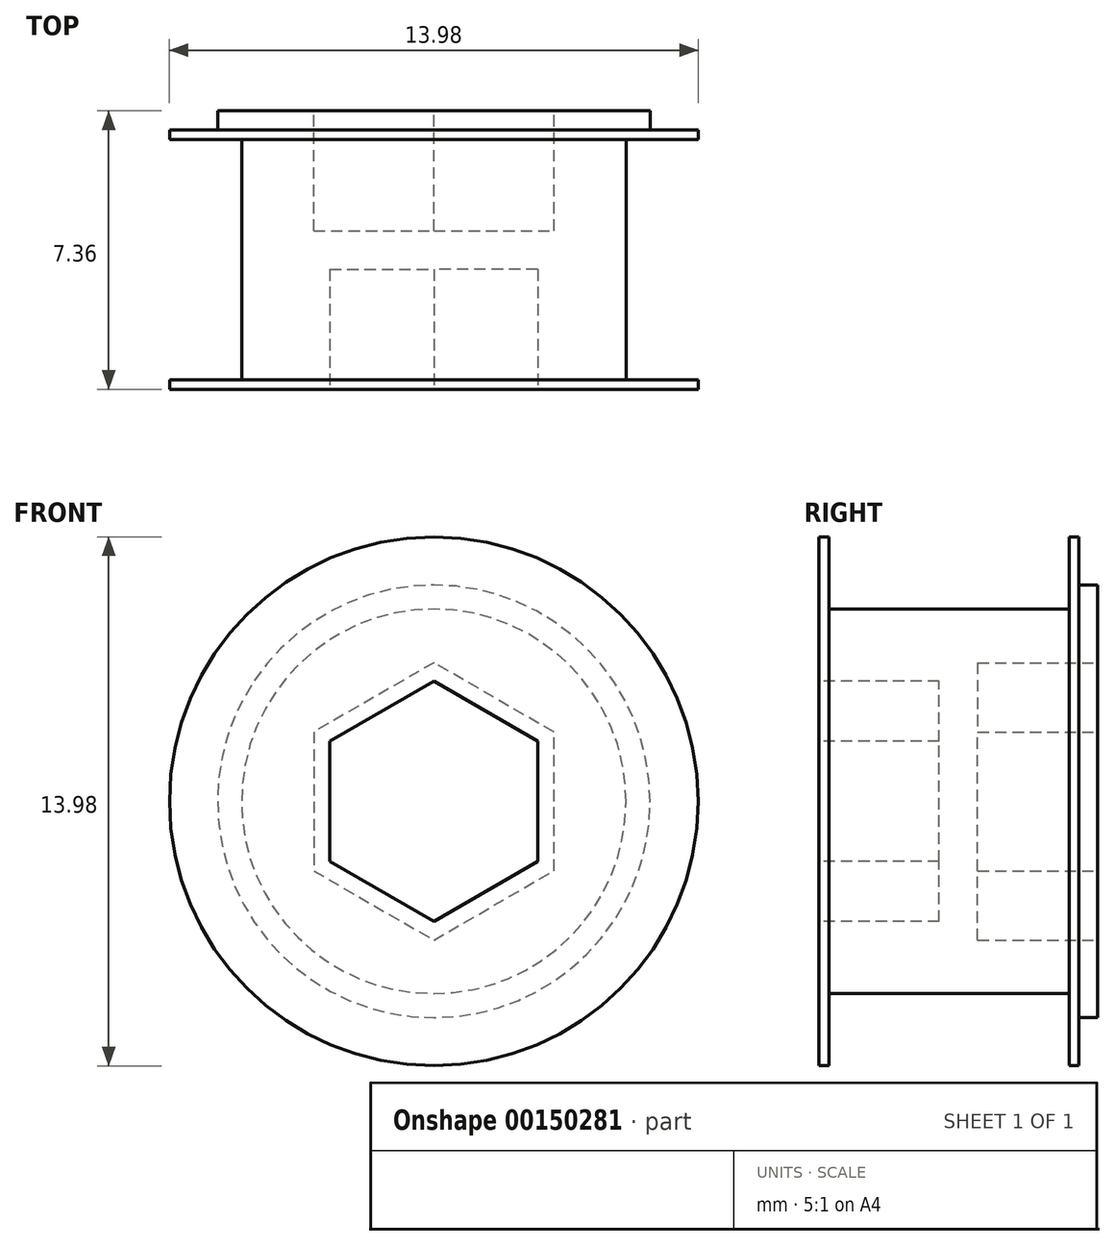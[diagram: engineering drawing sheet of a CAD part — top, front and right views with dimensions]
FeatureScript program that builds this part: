
annotation { "Feature Type Name" : "Feature", "Feature Type Description" : "" }
export const myFeature = defineFeature(function(context is Context, id is Id, definition is map)
    precondition{}
    {
        {
            var Q0;
            Q0=qCreatedBy(makeId("Front.planeOp"),FACE);
            var sketch = newSketch(context, id + "F0", { "sketchPlane" : qUnion([Q0])});
            skCircle(sketch, "E0", {"center": v(0, 0) * mm, "radius": 5.08 * mm});
            skSolve(sketch);
        }
        {
            var Q0;
            Q0 = qSketchRegion(id + "F0", true);
            extrude(context, id + "F1", {"entities" : qUnion([Q0]), "depth" : 6.35 * mm});
        }
        {
            var Q0;
            Q0=makeQuery(id+"F1.opExtrude","CAP_FACE",FACE,{"disambiguationData":[OSD([sQuery(id+"F0.wireOp",EDGE,"E0")])],"isStart":false});
            var sketch = newSketch(context, id + "F2", { "sketchPlane" : qUnion([Q0])});
            skCircle(sketch, "E1", {"center": v(0, 0) * mm, "radius": 6.99 * mm});
            skSolve(sketch);
        }
        {
            var Q0;
            Q0 = qSketchRegion(id + "F2", true);
            extrude(context, id + "F3", {"entities" : qUnion([Q0]), "operationType" : NewBodyOperationType.ADD, "depth" : 0.25 * mm});
        }
        {
            var Q0;
            Q0=qCreatedBy(makeId("Front.planeOp"),FACE);
            var sketch = newSketch(context, id + "F4", { "sketchPlane" : qUnion([Q0])});
            skCircle(sketch, "E2", {"center": v(0, 0) * mm, "radius": 6.99 * mm});
            skSolve(sketch);
        }
        {
            var Q0;
            Q0=makeQuery(id+"F4.imprint","IMPRINT",FACE,{"disambiguationData":[TD([[makeQuery(id+"F4.imprint","IMPRINT",EDGE,{"derivedFrom":sQuery(id+"F4.wireOp",EDGE,"E2")}),1.0]])]});
            extrude(context, id + "F5", {"entities" : qUnion([Q0]), "operationType" : NewBodyOperationType.ADD, "oppositeDirection" : true, "depth" : 0.25 * mm});
        }
        {
            var Q0;
            Q0=makeQuery(id+"F3.opExtrude","CAP_FACE",FACE,{"disambiguationData":[OSD([sQuery(id+"F2.wireOp",EDGE,"E1")])],"isStart":false});
            var sketch = newSketch(context, id + "F6", { "sketchPlane" : qUnion([Q0])});
            skCircle(sketch, "E3.cCircle", {"center": v(0, 0) * mm, "radius": 3.18 * mm, "construction": true});
            skLineSegment(sketch, "E3.0", {"start": v(-2.75, 1.59) * mm, "end": v(0, 3.18) * mm});
            skLineSegment(sketch, "E3.1", {"start": v(0, 3.18) * mm, "end": v(2.75, 1.59) * mm});
            skLineSegment(sketch, "E3.2", {"start": v(2.75, 1.59) * mm, "end": v(2.75, -1.59) * mm});
            skLineSegment(sketch, "E3.3", {"start": v(2.75, -1.59) * mm, "end": v(0, -3.18) * mm});
            skLineSegment(sketch, "E3.4", {"start": v(0, -3.18) * mm, "end": v(-2.75, -1.59) * mm});
            skLineSegment(sketch, "E3.5", {"start": v(-2.75, -1.59) * mm, "end": v(-2.75, 1.59) * mm});
            skSolve(sketch);
        }
        {
            var Q0;
            Q0=makeQuery(id+"F6.imprint","IMPRINT",FACE,{"disambiguationData":[TD([[makeQuery(id+"F6.imprint","IMPRINT",EDGE,{"derivedFrom":sQuery(id+"F6.wireOp",EDGE,"E3.0")}),-1.0]])]});
            extrude(context, id + "F7", {"entities" : qUnion([Q0]), "operationType" : NewBodyOperationType.REMOVE, "oppositeDirection" : true, "depth" : 3.17 * mm});
        }
        {
            var Q0;
            Q0=makeQuery(id+"F5.opExtrude","CAP_FACE",FACE,{"disambiguationData":[OSD([sQuery(id+"F4.wireOp",EDGE,"E2")])],"isStart":false});
            var sketch = newSketch(context, id + "F8", { "sketchPlane" : qUnion([Q0])});
            skCircle(sketch, "E4", {"center": v(0, 0) * mm, "radius": 5.72 * mm});
            skSolve(sketch);
        }
        {
            var Q0;
            Q0 = qSketchRegion(id + "F8", true);
            extrude(context, id + "F9", {"entities" : qUnion([Q0]), "operationType" : NewBodyOperationType.ADD, "depth" : 0.5 * mm});
        }
        {
            var Q0;
            Q0=makeQuery(id+"F9.opExtrude","CAP_FACE",FACE,{"disambiguationData":[OSD([sQuery(id+"F8.wireOp",EDGE,"E4")])],"isStart":false});
            var sketch = newSketch(context, id + "F10", { "sketchPlane" : qUnion([Q0])});
            skCircle(sketch, "E5.cCircle", {"center": v(0, 0) * mm, "radius": 3.18 * mm, "construction": true});
            skLineSegment(sketch, "E5.0", {"start": v(-3.18, -1.83) * mm, "end": v(-3.18, 1.83) * mm});
            skLineSegment(sketch, "E5.1", {"start": v(-3.18, 1.83) * mm, "end": v(0, 3.67) * mm});
            skLineSegment(sketch, "E5.2", {"start": v(0, 3.67) * mm, "end": v(3.17, 1.83) * mm});
            skLineSegment(sketch, "E5.3", {"start": v(3.17, 1.83) * mm, "end": v(3.18, -1.83) * mm});
            skLineSegment(sketch, "E5.4", {"start": v(3.18, -1.83) * mm, "end": v(0, -3.67) * mm});
            skLineSegment(sketch, "E5.5", {"start": v(0, -3.67) * mm, "end": v(-3.18, -1.83) * mm});
            skPoint(sketch, "E5.0.midPoint", {"position": v(-3.18, 0) * mm});
            skSolve(sketch);
        }
        {
            var Q0;
            Q0=makeQuery(id+"F10.imprint","IMPRINT",FACE,{"disambiguationData":[TD([[makeQuery(id+"F10.imprint","IMPRINT",EDGE,{"derivedFrom":sQuery(id+"F10.wireOp",EDGE,"E5.0")}),-1.0]])]});
            extrude(context, id + "F11", {"entities" : qUnion([Q0]), "operationType" : NewBodyOperationType.REMOVE, "oppositeDirection" : true, "depth" : 3.17 * mm});
        }
    });
